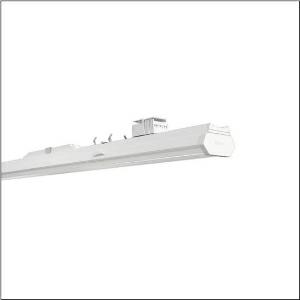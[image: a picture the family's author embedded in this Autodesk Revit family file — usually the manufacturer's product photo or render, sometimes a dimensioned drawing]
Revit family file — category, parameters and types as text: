
# Revit family: licross_r__11_protected_ho_51td1bdn4e5m3s4_89af
name_source: partatom
category: Lighting Fixtures
units: mm (PartAtom-declared; Revit-internal decimal feet)

## family parameters
Cut with Voids When Loaded = No
Host = Face
Light Source = No
Part Type = Normal
Room Calculation Point = No
Round Connector Dimension = Use Diameter
Shared = No

## types (1)
- --- (1 x LED, 920 lm, 7.4 W, 4000K)
    Apparent Load = 7 VA
    CIE Flux Codes = 54 82 95 97 100
    Color Rendering = 80
    Color Temperature = 4000K
    Default Elevation = 1800 mm
    Description = Licross® 11 Protected HO, luminaire insert, of sheet steel, galvanised, coil coated, white, length: 1.500mm, width: 90mm, height: 101mm, LED rated luminous flux: 14.500lm, light colour: 840, control gear: DALI 2, with plug, 6-pole, with phase selection, for trunking rail, 9 or 11-core, mains connection: 220..240V, AC, 50/60Hz, rated input power: 91W, for trunking rail, 9-/11-core, halogen-free wiring, for emergency light function, converter,control gear: single battery element, battery: LiFePO4, 9Ah, primary optical cover: cover, of PMMA, light emission: direct distribution, primary light characteristic: symmetric, protection rating (complete): IP54, insulation class (complete): insulation class I (protective earthing), certification: CE, UKCA, protection symbol: D if used in an environment with non-conductive dust loads with corresponding accessories, impact resistance: IK06, permissible ambient temperature for indoor applications: +5..+30°C, standard: EN 60598-2-22, LABS conformity tested according to VDMA 24364:2018-05, reducing of maximum allowable ambient temperature of 5°C with ceiling mounting, corresponds to IFS (International Featured Standards) requirements for safety and quality in the food industry, packaging unit: 1 piece
    Height = 92 mm
    Lamp = 1 x LED
    Lamp Light Flux = 920 lm
    Lamp Power = 7.4 W
    Lamp count = 1
    Length = 1500 mm
    Luminous efficacy = 124 lm/W
    Manufacturer = Siteco
    ModVariant = No
    Model = 51TD1BDN4E5M3S4
    Mounting Place = Ceiling
    Mounting Type = Pendant
    Number of Poles = 1
    OnlyDefault = Yes
    Power Factor = 1
    Product Name = Licross® 11 Protected HO
    Product group = luminaire insert
    ProductGroupID = 902
    Protection Class = Protection class I
    Protection Degree = IP 54
    RLX_Detail_Level = 1
    RLX_Emergency_Light_Flux = 0 lm
    RLX_Emergency_Type = 0
    RLX_Emergency_Type_DB = No
    RlxData = <blob elided: 24721 chars, md5=5cbb7e92>
    Socket = socket
    Standby Power = 0 W
    System Light Flux = 920 lm
    System Power = 7 W
    Type Comments = : emergency light operation: 3 h
    Type Image = l_1256145.jpg
    URL = http://relux.com
    VarID = @adj_091168
    Voltage = 0 V
    Weight = 0.00 kg
    Width = 88 mm

## geometry (parser evidence)
native form markers: Blend x4, Sweep x11
no freeform markers — native parametric forms only
